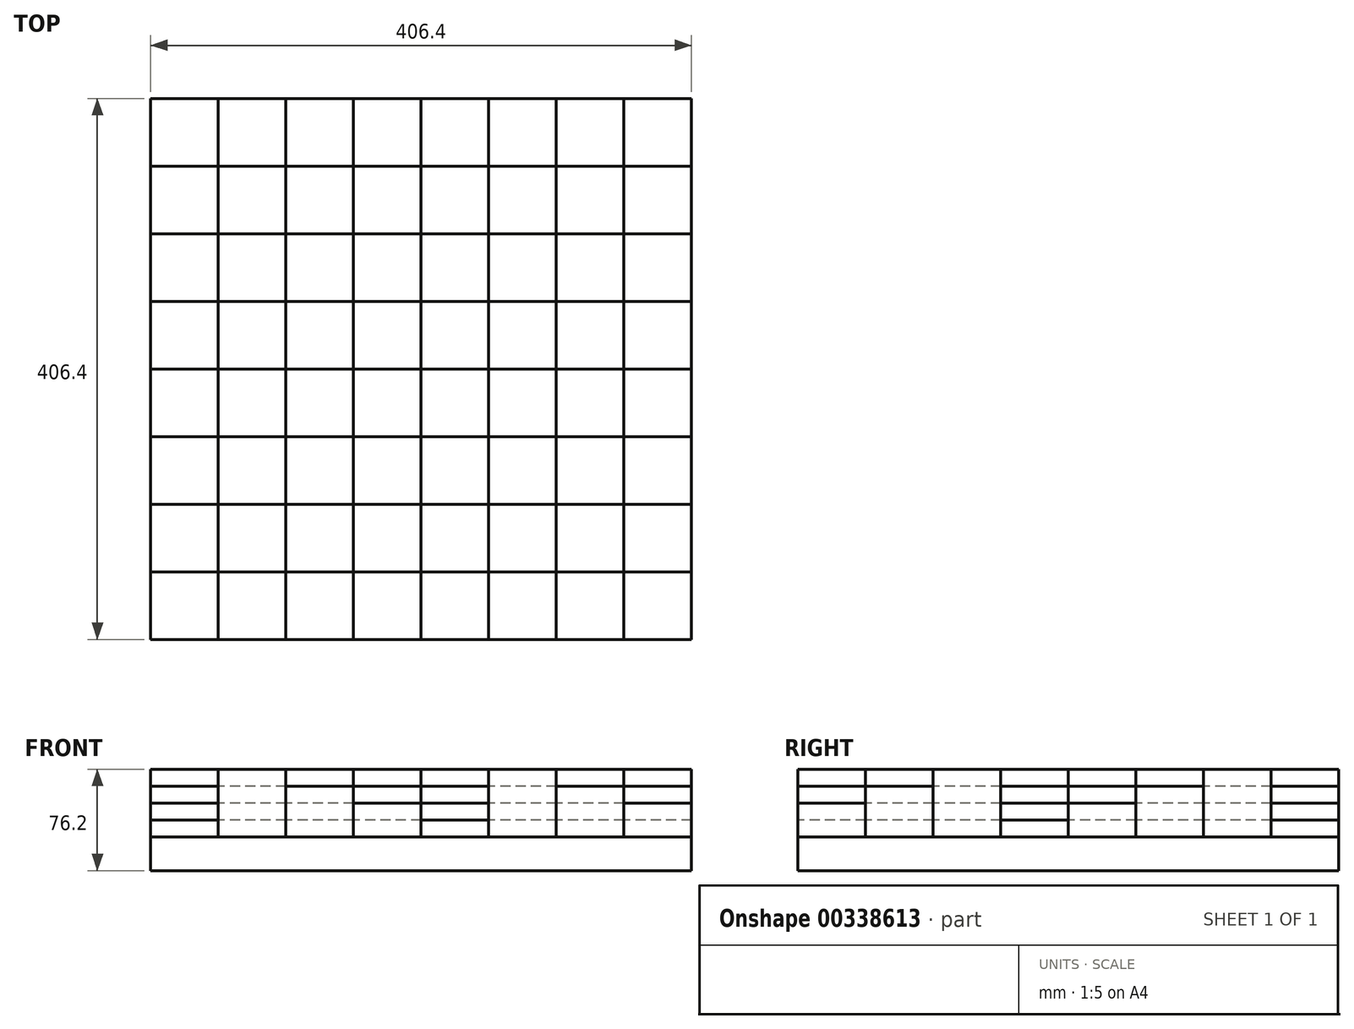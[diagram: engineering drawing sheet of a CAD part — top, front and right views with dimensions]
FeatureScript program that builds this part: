
annotation { "Feature Type Name" : "Feature", "Feature Type Description" : "" }
export const myFeature = defineFeature(function(context is Context, id is Id, definition is map)
    precondition{}
    {
        {
            var Q0;
            Q0=qCreatedBy(makeId("Top.planeOp"),FACE);
            var sketch = newSketch(context, id + "F0", { "sketchPlane" : qUnion([Q0])});
            skLineSegment(sketch, "E0.bottom", {"start": v(203.2, -203.2) * mm, "end": v(-203.2, -203.2) * mm});
            skLineSegment(sketch, "E0.top", {"start": v(203.2, 203.2) * mm, "end": v(-203.2, 203.2) * mm});
            skLineSegment(sketch, "E0.left", {"start": v(203.2, -203.2) * mm, "end": v(203.2, 203.2) * mm});
            skLineSegment(sketch, "E0.right", {"start": v(-203.2, -203.2) * mm, "end": v(-203.2, 203.2) * mm});
            skPoint(sketch, "E0.middle", {"position": v(0, 0) * mm});
            skSolve(sketch);
        }
        {
            var Q0;
            Q0=makeQuery(id+"F0.imprint","IMPRINT",FACE,{"disambiguationData":[TD([[makeQuery(id+"F0.imprint","IMPRINT",EDGE,{"derivedFrom":sQuery(id+"F0.wireOp",EDGE,"E0.bottom")}),-1.0]])]});
            extrude(context, id + "F1", {"entities" : qUnion([Q0]), "depth" : 25.4 * mm});
        }
        {
            var Q0;
            Q0=qCreatedBy(makeId("Right.planeOp"),FACE);
            var sketch = newSketch(context, id + "F2", { "sketchPlane" : qUnion([Q0])});
            skLineSegment(sketch, "E1", {"start": v(203.2, 25.4) * mm, "end": v(203.2, 76.2) * mm});
            skLineSegment(sketch, "E2", {"start": v(203.2, 76.2) * mm, "end": v(152.4, 76.2) * mm});
            skLineSegment(sketch, "E3", {"start": v(152.4, 76.2) * mm, "end": v(152.4, 25.4) * mm});
            skLineSegment(sketch, "E4", {"start": v(152.4, 25.4) * mm, "end": v(203.2, 25.4) * mm});
            skLineSegment(sketch, "E5", {"start": v(152.4, 63.5) * mm, "end": v(101.6, 63.5) * mm});
            skLineSegment(sketch, "E6", {"start": v(101.6, 63.5) * mm, "end": v(101.6, 25.4) * mm});
            skLineSegment(sketch, "E7", {"start": v(101.6, 25.4) * mm, "end": v(152.4, 25.4) * mm});
            skLineSegment(sketch, "E8.bottom", {"start": v(101.6, 25.4) * mm, "end": v(50.8, 25.4) * mm});
            skLineSegment(sketch, "E8.top", {"start": v(101.6, 50.8) * mm, "end": v(50.8, 50.8) * mm});
            skLineSegment(sketch, "E8.left", {"start": v(101.6, 25.4) * mm, "end": v(101.6, 50.8) * mm});
            skLineSegment(sketch, "E8.right", {"start": v(50.8, 25.4) * mm, "end": v(50.8, 50.8) * mm});
            skLineSegment(sketch, "E9.bottom", {"start": v(50.8, 25.4) * mm, "end": v(0, 25.4) * mm});
            skLineSegment(sketch, "E9.top", {"start": v(50.8, 38.1) * mm, "end": v(0, 38.1) * mm});
            skLineSegment(sketch, "E9.left", {"start": v(50.8, 25.4) * mm, "end": v(50.8, 38.1) * mm});
            skLineSegment(sketch, "E9.right", {"start": v(0, 25.4) * mm, "end": v(0, 38.1) * mm});
            skLineSegment(sketch, "E10.bottom", {"start": v(0, 25.4) * mm, "end": v(-50.8, 25.4) * mm});
            skLineSegment(sketch, "E10.top", {"start": v(0, 76.2) * mm, "end": v(-50.8, 76.2) * mm});
            skLineSegment(sketch, "E10.left", {"start": v(0, 25.4) * mm, "end": v(0, 76.2) * mm});
            skLineSegment(sketch, "E10.right", {"start": v(-50.8, 25.4) * mm, "end": v(-50.8, 76.2) * mm});
            skLineSegment(sketch, "E11.bottom", {"start": v(-50.8, 25.4) * mm, "end": v(-101.6, 25.4) * mm});
            skLineSegment(sketch, "E11.top", {"start": v(-50.8, 63.5) * mm, "end": v(-101.6, 63.5) * mm});
            skLineSegment(sketch, "E11.left", {"start": v(-50.8, 25.4) * mm, "end": v(-50.8, 63.5) * mm});
            skLineSegment(sketch, "E11.right", {"start": v(-101.6, 25.4) * mm, "end": v(-101.6, 63.5) * mm});
            skLineSegment(sketch, "E12.bottom", {"start": v(-101.6, 25.4) * mm, "end": v(-152.4, 25.4) * mm});
            skLineSegment(sketch, "E12.top", {"start": v(-101.6, 50.8) * mm, "end": v(-152.4, 50.8) * mm});
            skLineSegment(sketch, "E12.left", {"start": v(-101.6, 25.4) * mm, "end": v(-101.6, 50.8) * mm});
            skLineSegment(sketch, "E12.right", {"start": v(-152.4, 25.4) * mm, "end": v(-152.4, 50.8) * mm});
            skPoint(sketch, "E13.oppositeSnap0", {"position": v(-152.4, 38.1) * mm});
            skLineSegment(sketch, "E13.bottom", {"start": v(-152.4, 25.4) * mm, "end": v(-203.2, 25.4) * mm});
            skLineSegment(sketch, "E13.top", {"start": v(-152.4, 38.1) * mm, "end": v(-203.2, 38.1) * mm});
            skLineSegment(sketch, "E13.left", {"start": v(-152.4, 25.4) * mm, "end": v(-152.4, 38.1) * mm});
            skLineSegment(sketch, "E13.right", {"start": v(-203.2, 25.4) * mm, "end": v(-203.2, 38.1) * mm});
            skSolve(sketch);
        }
        {
            var Q0;
            Q0=makeQuery(id+"F2.imprint","IMPRINT",FACE,{"disambiguationData":[TD([[makeQuery(id+"F2.imprint","IMPRINT",EDGE,{"derivedFrom":sQuery(id+"F2.wireOp",EDGE,"E1")}),1.0]])]});
            extrude(context, id + "F3", {"entities" : qUnion([Q0]), "depth" : 50.8 * mm});
        }
        {
            var Q0;
            {var subQ1=sQuery(id+"F2.wireOp",EDGE,"E5");Q0=makeQuery(id+"F2.imprint","IMPRINT",FACE,{"disambiguationData":[TD([[makeQuery(id+"F2.imprint","IMPRINT",EDGE,{"derivedFrom":subQ1}),1.0]])]});}
            extrude(context, id + "F4", {"entities" : qUnion([Q0]), "depth" : 50.8 * mm});
        }
        {
            var Q0;
            Q0=makeQuery(id+"F2.imprint","IMPRINT",FACE,{"disambiguationData":[TD([[makeQuery(id+"F2.imprint","IMPRINT",EDGE,{"derivedFrom":sQuery(id+"F2.wireOp",EDGE,"E8.bottom")}),-1.0]])]});
            extrude(context, id + "F5", {"entities" : qUnion([Q0]), "depth" : 50.8 * mm});
        }
        {
            var Q0;
            Q0=makeQuery(id+"F2.imprint","IMPRINT",FACE,{"disambiguationData":[TD([[makeQuery(id+"F2.imprint","IMPRINT",EDGE,{"derivedFrom":sQuery(id+"F2.wireOp",EDGE,"E9.bottom")}),-1.0]])]});
            extrude(context, id + "F6", {"entities" : qUnion([Q0]), "depth" : 50.8 * mm});
        }
        {
            var Q0;
            Q0=qCreatedBy(makeId("Right.planeOp"),FACE);
            cPlane(context, id + "F7", {"entities" : qUnion([Q0]), "cplaneType" : CPlaneType.OFFSET, "offset" : 50.8 * mm, "width" : 152.4 * mm, "height" : 152.4 * mm});
        }
        {
            var Q0;
            Q0=qCreatedBy(makeId("Right.planeOp"),FACE);
            cPlane(context, id + "F8", {"entities" : qUnion([Q0]), "cplaneType" : CPlaneType.OFFSET, "offset" : 101.6 * mm, "width" : 152.4 * mm, "height" : 152.4 * mm});
        }
        {
            var Q0;
            Q0=qCreatedBy(makeId("Right.planeOp"),FACE);
            cPlane(context, id + "F9", {"entities" : qUnion([Q0]), "cplaneType" : CPlaneType.OFFSET, "offset" : 152.4 * mm, "width" : 152.4 * mm, "height" : 152.4 * mm});
        }
        {
            var Q0;
            {var subQ0=sQuery(id+"F2.wireOp",EDGE,"E10.bottom");Q0=makeQuery(id+"F2.imprint","IMPRINT",FACE,{"disambiguationData":[TD([[makeQuery(id+"F2.imprint","IMPRINT",EDGE,{"derivedFrom":subQ0}),-1.0]])]});}
            extrude(context, id + "F10", {"entities" : qUnion([Q0]), "depth" : 50.8 * mm});
        }
        {
            var Q0;
            {var subQ3=sQuery(id+"F2.wireOp",EDGE,"E11.bottom");Q0=makeQuery(id+"F2.imprint","IMPRINT",FACE,{"disambiguationData":[TD([[makeQuery(id+"F2.imprint","IMPRINT",EDGE,{"derivedFrom":subQ3}),-1.0]])]});}
            extrude(context, id + "F11", {"entities" : qUnion([Q0]), "depth" : 50.8 * mm});
        }
        {
            var Q0;
            {var subQ3=sQuery(id+"F2.wireOp",EDGE,"E13.bottom");Q0=makeQuery(id+"F2.imprint","IMPRINT",FACE,{"disambiguationData":[TD([[makeQuery(id+"F2.imprint","IMPRINT",EDGE,{"derivedFrom":subQ3}),-1.0]])]});}
            extrude(context, id + "F12", {"entities" : qUnion([Q0]), "depth" : 50.8 * mm});
        }
        {
            var Q0;
            {var subQ3=sQuery(id+"F2.wireOp",EDGE,"E12.bottom");Q0=makeQuery(id+"F2.imprint","IMPRINT",FACE,{"disambiguationData":[TD([[makeQuery(id+"F2.imprint","IMPRINT",EDGE,{"derivedFrom":subQ3}),-1.0]])]});}
            extrude(context, id + "F13", {"entities" : qUnion([Q0]), "depth" : 50.8 * mm});
        }
        {
            var Q0;
            Q0=qCreatedBy(id+"F7.planeOp",FACE);
            var sketch = newSketch(context, id + "F14", { "sketchPlane" : qUnion([Q0])});
            skLineSegment(sketch, "E14", {"start": v(203.2, 25.4) * mm, "end": v(203.2, 63.5) * mm});
            skLineSegment(sketch, "E15", {"start": v(203.2, 63.5) * mm, "end": v(152.4, 63.5) * mm});
            skLineSegment(sketch, "E16", {"start": v(152.4, 63.5) * mm, "end": v(152.4, 25.4) * mm});
            skLineSegment(sketch, "E17", {"start": v(152.4, 25.4) * mm, "end": v(203.2, 25.4) * mm});
            skLineSegment(sketch, "E18", {"start": v(152.4, 50.8) * mm, "end": v(101.6, 50.8) * mm});
            skLineSegment(sketch, "E19", {"start": v(101.6, 50.8) * mm, "end": v(101.6, 25.4) * mm});
            skLineSegment(sketch, "E20", {"start": v(101.6, 25.4) * mm, "end": v(152.4, 25.4) * mm});
            skLineSegment(sketch, "E21.bottom", {"start": v(101.6, 25.4) * mm, "end": v(50.8, 25.4) * mm});
            skLineSegment(sketch, "E21.top", {"start": v(101.6, 38.1) * mm, "end": v(50.8, 38.1) * mm});
            skLineSegment(sketch, "E21.left", {"start": v(101.6, 25.4) * mm, "end": v(101.6, 38.1) * mm});
            skLineSegment(sketch, "E21.right", {"start": v(50.8, 25.4) * mm, "end": v(50.8, 38.1) * mm});
            skLineSegment(sketch, "E22.bottom", {"start": v(50.8, 25.4) * mm, "end": v(0, 25.4) * mm});
            skLineSegment(sketch, "E22.top", {"start": v(50.8, 76.2) * mm, "end": v(0, 76.2) * mm});
            skLineSegment(sketch, "E22.left", {"start": v(50.8, 25.4) * mm, "end": v(50.8, 76.2) * mm});
            skLineSegment(sketch, "E22.right", {"start": v(0, 25.4) * mm, "end": v(0, 76.2) * mm});
            skLineSegment(sketch, "E23.bottom", {"start": v(0, 25.4) * mm, "end": v(-50.8, 25.4) * mm});
            skLineSegment(sketch, "E23.top", {"start": v(0, 63.5) * mm, "end": v(-50.8, 63.5) * mm});
            skLineSegment(sketch, "E23.left", {"start": v(0, 25.4) * mm, "end": v(0, 63.5) * mm});
            skLineSegment(sketch, "E23.right", {"start": v(-50.8, 25.4) * mm, "end": v(-50.8, 63.5) * mm});
            skLineSegment(sketch, "E24.bottom", {"start": v(-50.8, 25.4) * mm, "end": v(-101.6, 25.4) * mm});
            skLineSegment(sketch, "E24.top", {"start": v(-50.8, 50.8) * mm, "end": v(-101.6, 50.8) * mm});
            skLineSegment(sketch, "E24.left", {"start": v(-50.8, 25.4) * mm, "end": v(-50.8, 50.8) * mm});
            skLineSegment(sketch, "E24.right", {"start": v(-101.6, 25.4) * mm, "end": v(-101.6, 50.8) * mm});
            skLineSegment(sketch, "E25.bottom", {"start": v(-101.6, 25.4) * mm, "end": v(-152.4, 25.4) * mm});
            skLineSegment(sketch, "E25.top", {"start": v(-101.6, 38.1) * mm, "end": v(-152.4, 38.1) * mm});
            skLineSegment(sketch, "E25.left", {"start": v(-101.6, 25.4) * mm, "end": v(-101.6, 38.1) * mm});
            skLineSegment(sketch, "E25.right", {"start": v(-152.4, 25.4) * mm, "end": v(-152.4, 38.1) * mm});
            skPoint(sketch, "E26.oppositeSnap0", {"position": v(-152.4, 31.75) * mm});
            skLineSegment(sketch, "E26.bottom", {"start": v(-152.4, 25.4) * mm, "end": v(-203.2, 25.4) * mm});
            skLineSegment(sketch, "E26.top", {"start": v(-152.4, 76.2) * mm, "end": v(-203.2, 76.2) * mm});
            skLineSegment(sketch, "E26.left", {"start": v(-152.4, 25.4) * mm, "end": v(-152.4, 76.2) * mm});
            skLineSegment(sketch, "E26.right", {"start": v(-203.2, 25.4) * mm, "end": v(-203.2, 76.2) * mm});
            skSolve(sketch);
        }
        {
            var Q0;
            Q0=makeQuery(id+"F14.imprint","IMPRINT",FACE,{"disambiguationData":[TD([[makeQuery(id+"F14.imprint","IMPRINT",EDGE,{"derivedFrom":sQuery(id+"F14.wireOp",EDGE,"E14")}),1.0]])]});
            extrude(context, id + "F15", {"entities" : qUnion([Q0]), "depth" : 50.8 * mm});
        }
        {
            var Q0;
            {var subQ1=sQuery(id+"F14.wireOp",EDGE,"E18");Q0=makeQuery(id+"F14.imprint","IMPRINT",FACE,{"disambiguationData":[TD([[makeQuery(id+"F14.imprint","IMPRINT",EDGE,{"derivedFrom":subQ1}),1.0]])]});}
            extrude(context, id + "F16", {"entities" : qUnion([Q0]), "depth" : 50.8 * mm});
        }
        {
            var Q0;
            {var subQ0=sQuery(id+"F14.wireOp",EDGE,"E21.bottom");Q0=makeQuery(id+"F14.imprint","IMPRINT",FACE,{"disambiguationData":[TD([[makeQuery(id+"F14.imprint","IMPRINT",EDGE,{"derivedFrom":subQ0}),-1.0]])]});}
            extrude(context, id + "F17", {"entities" : qUnion([Q0]), "depth" : 50.8 * mm});
        }
        {
            var Q0;
            {var subQ3=sQuery(id+"F14.wireOp",EDGE,"E22.bottom");Q0=makeQuery(id+"F14.imprint","IMPRINT",FACE,{"disambiguationData":[TD([[makeQuery(id+"F14.imprint","IMPRINT",EDGE,{"derivedFrom":subQ3}),-1.0]])]});}
            extrude(context, id + "F18", {"entities" : qUnion([Q0]), "depth" : 50.8 * mm});
        }
        {
            var Q0;
            Q0=makeQuery(id+"F14.imprint","IMPRINT",FACE,{"disambiguationData":[TD([[makeQuery(id+"F14.imprint","IMPRINT",EDGE,{"derivedFrom":sQuery(id+"F14.wireOp",EDGE,"E23.bottom")}),-1.0]])]});
            extrude(context, id + "F19", {"entities" : qUnion([Q0]), "depth" : 50.8 * mm});
        }
        {
            var Q0;
            Q0=makeQuery(id+"F14.imprint","IMPRINT",FACE,{"disambiguationData":[TD([[makeQuery(id+"F14.imprint","IMPRINT",EDGE,{"derivedFrom":sQuery(id+"F14.wireOp",EDGE,"E24.bottom")}),-1.0]])]});
            extrude(context, id + "F20", {"entities" : qUnion([Q0]), "depth" : 50.8 * mm});
        }
        {
            var Q0;
            {var subQ0=sQuery(id+"F14.wireOp",EDGE,"E25.bottom");Q0=makeQuery(id+"F14.imprint","IMPRINT",FACE,{"disambiguationData":[TD([[makeQuery(id+"F14.imprint","IMPRINT",EDGE,{"derivedFrom":subQ0}),-1.0]])]});}
            extrude(context, id + "F21", {"entities" : qUnion([Q0]), "depth" : 50.8 * mm});
        }
        {
            var Q0;
            {var subQ3=sQuery(id+"F14.wireOp",EDGE,"E26.bottom");Q0=makeQuery(id+"F14.imprint","IMPRINT",FACE,{"disambiguationData":[TD([[makeQuery(id+"F14.imprint","IMPRINT",EDGE,{"derivedFrom":subQ3}),-1.0]])]});}
            extrude(context, id + "F22", {"entities" : qUnion([Q0]), "depth" : 50.8 * mm});
        }
        {
            var Q0;
            Q0=qCreatedBy(id+"F8.planeOp",FACE);
            var sketch = newSketch(context, id + "F23", { "sketchPlane" : qUnion([Q0])});
            skLineSegment(sketch, "E27", {"start": v(203.2, 25.4) * mm, "end": v(203.2, 50.8) * mm});
            skLineSegment(sketch, "E28", {"start": v(203.2, 50.8) * mm, "end": v(152.4, 50.8) * mm});
            skLineSegment(sketch, "E29", {"start": v(152.4, 50.8) * mm, "end": v(152.4, 25.4) * mm});
            skLineSegment(sketch, "E30", {"start": v(152.4, 25.4) * mm, "end": v(203.2, 25.4) * mm});
            skLineSegment(sketch, "E31", {"start": v(152.4, 38.1) * mm, "end": v(101.6, 38.1) * mm});
            skLineSegment(sketch, "E32", {"start": v(101.6, 38.1) * mm, "end": v(101.6, 25.4) * mm});
            skLineSegment(sketch, "E33", {"start": v(101.6, 25.4) * mm, "end": v(152.4, 25.4) * mm});
            skLineSegment(sketch, "E34.bottom", {"start": v(101.6, 25.4) * mm, "end": v(50.8, 25.4) * mm});
            skLineSegment(sketch, "E34.top", {"start": v(101.6, 76.2) * mm, "end": v(50.8, 76.2) * mm});
            skLineSegment(sketch, "E34.left", {"start": v(101.6, 25.4) * mm, "end": v(101.6, 76.2) * mm});
            skLineSegment(sketch, "E34.right", {"start": v(50.8, 25.4) * mm, "end": v(50.8, 76.2) * mm});
            skLineSegment(sketch, "E35.bottom", {"start": v(50.8, 25.4) * mm, "end": v(0, 25.4) * mm});
            skLineSegment(sketch, "E35.top", {"start": v(50.8, 63.5) * mm, "end": v(0, 63.5) * mm});
            skLineSegment(sketch, "E35.left", {"start": v(50.8, 25.4) * mm, "end": v(50.8, 63.5) * mm});
            skLineSegment(sketch, "E35.right", {"start": v(0, 25.4) * mm, "end": v(0, 63.5) * mm});
            skLineSegment(sketch, "E36.bottom", {"start": v(0, 25.4) * mm, "end": v(-50.8, 25.4) * mm});
            skLineSegment(sketch, "E36.top", {"start": v(0, 50.8) * mm, "end": v(-50.8, 50.8) * mm});
            skLineSegment(sketch, "E36.left", {"start": v(0, 25.4) * mm, "end": v(0, 50.8) * mm});
            skLineSegment(sketch, "E36.right", {"start": v(-50.8, 25.4) * mm, "end": v(-50.8, 50.8) * mm});
            skLineSegment(sketch, "E37.bottom", {"start": v(-50.8, 25.4) * mm, "end": v(-101.6, 25.4) * mm});
            skLineSegment(sketch, "E37.top", {"start": v(-50.8, 38.1) * mm, "end": v(-101.6, 38.1) * mm});
            skLineSegment(sketch, "E37.left", {"start": v(-50.8, 25.4) * mm, "end": v(-50.8, 38.1) * mm});
            skLineSegment(sketch, "E37.right", {"start": v(-101.6, 25.4) * mm, "end": v(-101.6, 38.1) * mm});
            skLineSegment(sketch, "E38.bottom", {"start": v(-101.6, 25.4) * mm, "end": v(-152.4, 25.4) * mm});
            skLineSegment(sketch, "E38.top", {"start": v(-101.6, 76.2) * mm, "end": v(-152.4, 76.2) * mm});
            skLineSegment(sketch, "E38.left", {"start": v(-101.6, 25.4) * mm, "end": v(-101.6, 76.2) * mm});
            skLineSegment(sketch, "E38.right", {"start": v(-152.4, 25.4) * mm, "end": v(-152.4, 76.2) * mm});
            skPoint(sketch, "E39.oppositeSnap0", {"position": v(-152.4, 50.8) * mm});
            skLineSegment(sketch, "E39.bottom", {"start": v(-152.4, 25.4) * mm, "end": v(-203.2, 25.4) * mm});
            skLineSegment(sketch, "E39.top", {"start": v(-152.4, 63.5) * mm, "end": v(-203.2, 63.5) * mm});
            skLineSegment(sketch, "E39.left", {"start": v(-152.4, 25.4) * mm, "end": v(-152.4, 63.5) * mm});
            skLineSegment(sketch, "E39.right", {"start": v(-203.2, 25.4) * mm, "end": v(-203.2, 63.5) * mm});
            skSolve(sketch);
        }
        {
            var Q0;
            Q0=makeQuery(id+"F23.imprint","IMPRINT",FACE,{"disambiguationData":[TD([[makeQuery(id+"F23.imprint","IMPRINT",EDGE,{"derivedFrom":sQuery(id+"F23.wireOp",EDGE,"E27")}),1.0]])]});
            var Q1;
            {var subQ3=sQuery(id+"F23.wireOp",EDGE,"E34.bottom");Q1=makeQuery(id+"F23.imprint","IMPRINT",FACE,{"disambiguationData":[TD([[makeQuery(id+"F23.imprint","IMPRINT",EDGE,{"derivedFrom":subQ3}),-1.0]])]});}
            var Q2;
            Q2=makeQuery(id+"F23.imprint","IMPRINT",FACE,{"disambiguationData":[TD([[makeQuery(id+"F23.imprint","IMPRINT",EDGE,{"derivedFrom":sQuery(id+"F23.wireOp",EDGE,"E36.bottom")}),-1.0]])]});
            var Q3;
            {var subQ3=sQuery(id+"F23.wireOp",EDGE,"E38.bottom");Q3=makeQuery(id+"F23.imprint","IMPRINT",FACE,{"disambiguationData":[TD([[makeQuery(id+"F23.imprint","IMPRINT",EDGE,{"derivedFrom":subQ3}),-1.0]])]});}
            extrude(context, id + "F24", {"entities" : qUnion([Q0, Q1, Q2, Q3]), "depth" : 50.8 * mm});
        }
        {
            var Q0;
            {var subQ2=sQuery(id+"F23.wireOp",EDGE,"E31");Q0=makeQuery(id+"F23.imprint","IMPRINT",FACE,{"disambiguationData":[TD([[makeQuery(id+"F23.imprint","IMPRINT",EDGE,{"derivedFrom":subQ2}),1.0]])]});}
            var Q1;
            Q1=makeQuery(id+"F23.imprint","IMPRINT",FACE,{"disambiguationData":[TD([[makeQuery(id+"F23.imprint","IMPRINT",EDGE,{"derivedFrom":sQuery(id+"F23.wireOp",EDGE,"E35.bottom")}),-1.0]])]});
            var Q2;
            {var subQ0=sQuery(id+"F23.wireOp",EDGE,"E37.bottom");Q2=makeQuery(id+"F23.imprint","IMPRINT",FACE,{"disambiguationData":[TD([[makeQuery(id+"F23.imprint","IMPRINT",EDGE,{"derivedFrom":subQ0}),-1.0]])]});}
            var Q3;
            Q3=makeQuery(id+"F23.imprint","IMPRINT",FACE,{"disambiguationData":[TD([[makeQuery(id+"F23.imprint","IMPRINT",EDGE,{"derivedFrom":sQuery(id+"F23.wireOp",EDGE,"E39.bottom")}),-1.0]])]});
            extrude(context, id + "F25", {"entities" : qUnion([Q0, Q1, Q2, Q3]), "depth" : 50.8 * mm});
        }
        {
            var Q0;
            Q0=qCreatedBy(id+"F9.planeOp",FACE);
            var sketch = newSketch(context, id + "F26", { "sketchPlane" : qUnion([Q0])});
            skLineSegment(sketch, "E40", {"start": v(203.2, 25.4) * mm, "end": v(203.2, 38.1) * mm});
            skLineSegment(sketch, "E41", {"start": v(203.2, 38.1) * mm, "end": v(152.4, 38.1) * mm});
            skLineSegment(sketch, "E42", {"start": v(152.4, 38.1) * mm, "end": v(152.4, 25.4) * mm});
            skLineSegment(sketch, "E43", {"start": v(152.4, 25.4) * mm, "end": v(203.2, 25.4) * mm});
            skLineSegment(sketch, "E44", {"start": v(152.4, 76.2) * mm, "end": v(101.6, 76.2) * mm});
            skLineSegment(sketch, "E45", {"start": v(101.6, 76.2) * mm, "end": v(101.6, 25.4) * mm});
            skLineSegment(sketch, "E46", {"start": v(101.6, 25.4) * mm, "end": v(152.4, 25.4) * mm});
            skLineSegment(sketch, "E47.bottom", {"start": v(101.6, 25.4) * mm, "end": v(50.8, 25.4) * mm});
            skLineSegment(sketch, "E47.top", {"start": v(101.6, 63.5) * mm, "end": v(50.8, 63.5) * mm});
            skLineSegment(sketch, "E47.left", {"start": v(101.6, 25.4) * mm, "end": v(101.6, 63.5) * mm});
            skLineSegment(sketch, "E47.right", {"start": v(50.8, 25.4) * mm, "end": v(50.8, 63.5) * mm});
            skLineSegment(sketch, "E48.bottom", {"start": v(50.8, 25.4) * mm, "end": v(0, 25.4) * mm});
            skLineSegment(sketch, "E48.top", {"start": v(50.8, 50.8) * mm, "end": v(0, 50.8) * mm});
            skLineSegment(sketch, "E48.left", {"start": v(50.8, 25.4) * mm, "end": v(50.8, 50.8) * mm});
            skLineSegment(sketch, "E48.right", {"start": v(0, 25.4) * mm, "end": v(0, 50.8) * mm});
            skLineSegment(sketch, "E49.bottom", {"start": v(0, 25.4) * mm, "end": v(-50.8, 25.4) * mm});
            skLineSegment(sketch, "E49.top", {"start": v(0, 38.1) * mm, "end": v(-50.8, 38.1) * mm});
            skLineSegment(sketch, "E49.left", {"start": v(0, 25.4) * mm, "end": v(0, 38.1) * mm});
            skLineSegment(sketch, "E49.right", {"start": v(-50.8, 25.4) * mm, "end": v(-50.8, 38.1) * mm});
            skLineSegment(sketch, "E50.bottom", {"start": v(-50.8, 25.4) * mm, "end": v(-101.6, 25.4) * mm});
            skLineSegment(sketch, "E50.top", {"start": v(-50.8, 76.2) * mm, "end": v(-101.6, 76.2) * mm});
            skLineSegment(sketch, "E50.left", {"start": v(-50.8, 25.4) * mm, "end": v(-50.8, 76.2) * mm});
            skLineSegment(sketch, "E50.right", {"start": v(-101.6, 25.4) * mm, "end": v(-101.6, 76.2) * mm});
            skLineSegment(sketch, "E51.bottom", {"start": v(-101.6, 25.4) * mm, "end": v(-152.4, 25.4) * mm});
            skLineSegment(sketch, "E51.top", {"start": v(-101.6, 63.5) * mm, "end": v(-152.4, 63.5) * mm});
            skLineSegment(sketch, "E51.left", {"start": v(-101.6, 25.4) * mm, "end": v(-101.6, 63.5) * mm});
            skLineSegment(sketch, "E51.right", {"start": v(-152.4, 25.4) * mm, "end": v(-152.4, 63.5) * mm});
            skPoint(sketch, "E52.oppositeSnap0", {"position": v(-152.4, 44.45) * mm});
            skLineSegment(sketch, "E52.bottom", {"start": v(-152.4, 25.4) * mm, "end": v(-203.2, 25.4) * mm});
            skLineSegment(sketch, "E52.top", {"start": v(-152.4, 50.8) * mm, "end": v(-203.2, 50.8) * mm});
            skLineSegment(sketch, "E52.left", {"start": v(-152.4, 25.4) * mm, "end": v(-152.4, 50.8) * mm});
            skLineSegment(sketch, "E52.right", {"start": v(-203.2, 25.4) * mm, "end": v(-203.2, 50.8) * mm});
            skLineSegment(sketch, "E53", {"start": v(152.4, 38.1) * mm, "end": v(152.4, 76.2) * mm});
            skSolve(sketch);
        }
        {
            var Q0;
            Q0=makeQuery(id+"F26.imprint","IMPRINT",FACE,{"disambiguationData":[TD([[makeQuery(id+"F26.imprint","IMPRINT",EDGE,{"derivedFrom":sQuery(id+"F26.wireOp",EDGE,"E40")}),1.0]])]});
            var Q1;
            Q1=makeQuery(id+"F26.imprint","IMPRINT",FACE,{"disambiguationData":[TD([[makeQuery(id+"F26.imprint","IMPRINT",EDGE,{"derivedFrom":sQuery(id+"F26.wireOp",EDGE,"E47.bottom")}),-1.0]])]});
            var Q2;
            {var subQ0=sQuery(id+"F26.wireOp",EDGE,"E49.bottom");Q2=makeQuery(id+"F26.imprint","IMPRINT",FACE,{"disambiguationData":[TD([[makeQuery(id+"F26.imprint","IMPRINT",EDGE,{"derivedFrom":subQ0}),-1.0]])]});}
            var Q3;
            Q3=makeQuery(id+"F26.imprint","IMPRINT",FACE,{"disambiguationData":[TD([[makeQuery(id+"F26.imprint","IMPRINT",EDGE,{"derivedFrom":sQuery(id+"F26.wireOp",EDGE,"E51.bottom")}),-1.0]])]});
            extrude(context, id + "F27", {"entities" : qUnion([Q0, Q1, Q2, Q3]), "depth" : 50.8 * mm});
        }
        {
            var Q0;
            Q0=makeQuery(id+"F26.imprint","IMPRINT",FACE,{"disambiguationData":[TD([[makeQuery(id+"F26.imprint","IMPRINT",EDGE,{"derivedFrom":sQuery(id+"F26.wireOp",EDGE,"E42")}),-1.0]])]});
            var Q1;
            Q1=makeQuery(id+"F26.imprint","IMPRINT",FACE,{"disambiguationData":[TD([[makeQuery(id+"F26.imprint","IMPRINT",EDGE,{"derivedFrom":sQuery(id+"F26.wireOp",EDGE,"E48.bottom")}),-1.0]])]});
            var Q2;
            {var subQ3=sQuery(id+"F26.wireOp",EDGE,"E50.bottom");Q2=makeQuery(id+"F26.imprint","IMPRINT",FACE,{"disambiguationData":[TD([[makeQuery(id+"F26.imprint","IMPRINT",EDGE,{"derivedFrom":subQ3}),-1.0]])]});}
            var Q3;
            Q3=makeQuery(id+"F26.imprint","IMPRINT",FACE,{"disambiguationData":[TD([[makeQuery(id+"F26.imprint","IMPRINT",EDGE,{"derivedFrom":sQuery(id+"F26.wireOp",EDGE,"E52.bottom")}),-1.0]])]});
            extrude(context, id + "F28", {"entities" : qUnion([Q0, Q1, Q2, Q3]), "depth" : 50.8 * mm});
        }
        {
            var Q0;
            Q0=qCreatedBy(makeId("Right.planeOp"),FACE);
            cPlane(context, id + "F29", {"entities" : qUnion([Q0]), "cplaneType" : CPlaneType.OFFSET, "offset" : 50.8 * mm, "oppositeDirection" : true, "width" : 152.4 * mm, "height" : 152.4 * mm});
        }
        {
            var Q0;
            Q0=qCreatedBy(makeId("Right.planeOp"),FACE);
            cPlane(context, id + "F30", {"entities" : qUnion([Q0]), "cplaneType" : CPlaneType.OFFSET, "offset" : 101.6 * mm, "oppositeDirection" : true, "width" : 152.4 * mm, "height" : 152.4 * mm});
        }
        {
            var Q0;
            Q0=qCreatedBy(makeId("Right.planeOp"),FACE);
            cPlane(context, id + "F31", {"entities" : qUnion([Q0]), "cplaneType" : CPlaneType.OFFSET, "offset" : 152.4 * mm, "oppositeDirection" : true, "width" : 152.4 * mm, "height" : 152.4 * mm});
        }
        {
            var Q0;
            Q0=qCreatedBy(id+"F29.planeOp",FACE);
            var sketch = newSketch(context, id + "F32", { "sketchPlane" : qUnion([Q0])});
            skLineSegment(sketch, "E54", {"start": v(203.2, 25.4) * mm, "end": v(203.2, 38.1) * mm});
            skLineSegment(sketch, "E55", {"start": v(203.2, 38.1) * mm, "end": v(152.4, 38.1) * mm});
            skLineSegment(sketch, "E56", {"start": v(152.4, 38.1) * mm, "end": v(152.4, 25.4) * mm});
            skLineSegment(sketch, "E57", {"start": v(152.4, 25.4) * mm, "end": v(203.2, 25.4) * mm});
            skLineSegment(sketch, "E58", {"start": v(152.4, 76.2) * mm, "end": v(101.6, 76.2) * mm});
            skLineSegment(sketch, "E59", {"start": v(101.6, 76.2) * mm, "end": v(101.6, 25.4) * mm});
            skLineSegment(sketch, "E60", {"start": v(101.6, 25.4) * mm, "end": v(152.4, 25.4) * mm});
            skLineSegment(sketch, "E61.bottom", {"start": v(101.6, 25.4) * mm, "end": v(50.8, 25.4) * mm});
            skLineSegment(sketch, "E61.top", {"start": v(101.6, 63.5) * mm, "end": v(50.8, 63.5) * mm});
            skLineSegment(sketch, "E61.left", {"start": v(101.6, 25.4) * mm, "end": v(101.6, 63.5) * mm});
            skLineSegment(sketch, "E61.right", {"start": v(50.8, 25.4) * mm, "end": v(50.8, 63.5) * mm});
            skLineSegment(sketch, "E62.bottom", {"start": v(50.8, 25.4) * mm, "end": v(0, 25.4) * mm});
            skLineSegment(sketch, "E62.top", {"start": v(50.8, 50.8) * mm, "end": v(0, 50.8) * mm});
            skLineSegment(sketch, "E62.left", {"start": v(50.8, 25.4) * mm, "end": v(50.8, 50.8) * mm});
            skLineSegment(sketch, "E62.right", {"start": v(0, 25.4) * mm, "end": v(0, 50.8) * mm});
            skLineSegment(sketch, "E63.bottom", {"start": v(0, 25.4) * mm, "end": v(-50.8, 25.4) * mm});
            skLineSegment(sketch, "E63.top", {"start": v(0, 38.1) * mm, "end": v(-50.8, 38.1) * mm});
            skLineSegment(sketch, "E63.left", {"start": v(0, 25.4) * mm, "end": v(0, 38.1) * mm});
            skLineSegment(sketch, "E63.right", {"start": v(-50.8, 25.4) * mm, "end": v(-50.8, 38.1) * mm});
            skLineSegment(sketch, "E64.bottom", {"start": v(-50.8, 25.4) * mm, "end": v(-101.6, 25.4) * mm});
            skLineSegment(sketch, "E64.top", {"start": v(-50.8, 76.2) * mm, "end": v(-101.6, 76.2) * mm});
            skLineSegment(sketch, "E64.left", {"start": v(-50.8, 25.4) * mm, "end": v(-50.8, 76.2) * mm});
            skLineSegment(sketch, "E64.right", {"start": v(-101.6, 25.4) * mm, "end": v(-101.6, 76.2) * mm});
            skLineSegment(sketch, "E65.bottom", {"start": v(-101.6, 25.4) * mm, "end": v(-152.4, 25.4) * mm});
            skLineSegment(sketch, "E65.top", {"start": v(-101.6, 63.5) * mm, "end": v(-152.4, 63.5) * mm});
            skLineSegment(sketch, "E65.left", {"start": v(-101.6, 25.4) * mm, "end": v(-101.6, 63.5) * mm});
            skLineSegment(sketch, "E65.right", {"start": v(-152.4, 25.4) * mm, "end": v(-152.4, 63.5) * mm});
            skPoint(sketch, "E66.oppositeSnap0", {"position": v(-152.4, 44.45) * mm});
            skLineSegment(sketch, "E66.bottom", {"start": v(-152.4, 25.4) * mm, "end": v(-203.2, 25.4) * mm});
            skLineSegment(sketch, "E66.top", {"start": v(-152.4, 50.8) * mm, "end": v(-203.2, 50.8) * mm});
            skLineSegment(sketch, "E66.left", {"start": v(-152.4, 25.4) * mm, "end": v(-152.4, 50.8) * mm});
            skLineSegment(sketch, "E66.right", {"start": v(-203.2, 25.4) * mm, "end": v(-203.2, 50.8) * mm});
            skLineSegment(sketch, "E67", {"start": v(152.4, 38.1) * mm, "end": v(152.4, 76.2) * mm});
            skSolve(sketch);
        }
        {
            var Q0;
            Q0=qCreatedBy(id+"F30.planeOp",FACE);
            var sketch = newSketch(context, id + "F33", { "sketchPlane" : qUnion([Q0])});
            skLineSegment(sketch, "E68", {"start": v(203.2, 25.4) * mm, "end": v(203.2, 50.8) * mm});
            skLineSegment(sketch, "E69", {"start": v(203.2, 50.8) * mm, "end": v(152.4, 50.8) * mm});
            skLineSegment(sketch, "E70", {"start": v(152.4, 50.8) * mm, "end": v(152.4, 25.4) * mm});
            skLineSegment(sketch, "E71", {"start": v(152.4, 25.4) * mm, "end": v(203.2, 25.4) * mm});
            skLineSegment(sketch, "E72", {"start": v(152.4, 38.1) * mm, "end": v(101.6, 38.1) * mm});
            skLineSegment(sketch, "E73", {"start": v(101.6, 38.1) * mm, "end": v(101.6, 25.4) * mm});
            skLineSegment(sketch, "E74", {"start": v(101.6, 25.4) * mm, "end": v(152.4, 25.4) * mm});
            skLineSegment(sketch, "E75.bottom", {"start": v(101.6, 25.4) * mm, "end": v(50.8, 25.4) * mm});
            skLineSegment(sketch, "E75.top", {"start": v(101.6, 76.2) * mm, "end": v(50.8, 76.2) * mm});
            skLineSegment(sketch, "E75.left", {"start": v(101.6, 25.4) * mm, "end": v(101.6, 76.2) * mm});
            skLineSegment(sketch, "E75.right", {"start": v(50.8, 25.4) * mm, "end": v(50.8, 76.2) * mm});
            skLineSegment(sketch, "E76.bottom", {"start": v(50.8, 25.4) * mm, "end": v(0, 25.4) * mm});
            skLineSegment(sketch, "E76.top", {"start": v(50.8, 63.5) * mm, "end": v(0, 63.5) * mm});
            skLineSegment(sketch, "E76.left", {"start": v(50.8, 25.4) * mm, "end": v(50.8, 63.5) * mm});
            skLineSegment(sketch, "E76.right", {"start": v(0, 25.4) * mm, "end": v(0, 63.5) * mm});
            skLineSegment(sketch, "E77.bottom", {"start": v(0, 25.4) * mm, "end": v(-50.8, 25.4) * mm});
            skLineSegment(sketch, "E77.top", {"start": v(0, 50.8) * mm, "end": v(-50.8, 50.8) * mm});
            skLineSegment(sketch, "E77.left", {"start": v(0, 25.4) * mm, "end": v(0, 50.8) * mm});
            skLineSegment(sketch, "E77.right", {"start": v(-50.8, 25.4) * mm, "end": v(-50.8, 50.8) * mm});
            skLineSegment(sketch, "E78.bottom", {"start": v(-50.8, 25.4) * mm, "end": v(-101.6, 25.4) * mm});
            skLineSegment(sketch, "E78.top", {"start": v(-50.8, 38.1) * mm, "end": v(-101.6, 38.1) * mm});
            skLineSegment(sketch, "E78.left", {"start": v(-50.8, 25.4) * mm, "end": v(-50.8, 38.1) * mm});
            skLineSegment(sketch, "E78.right", {"start": v(-101.6, 25.4) * mm, "end": v(-101.6, 38.1) * mm});
            skLineSegment(sketch, "E79.bottom", {"start": v(-101.6, 25.4) * mm, "end": v(-152.4, 25.4) * mm});
            skLineSegment(sketch, "E79.top", {"start": v(-101.6, 76.2) * mm, "end": v(-152.4, 76.2) * mm});
            skLineSegment(sketch, "E79.left", {"start": v(-101.6, 25.4) * mm, "end": v(-101.6, 76.2) * mm});
            skLineSegment(sketch, "E79.right", {"start": v(-152.4, 25.4) * mm, "end": v(-152.4, 76.2) * mm});
            skPoint(sketch, "E80.oppositeSnap0", {"position": v(-152.4, 50.8) * mm});
            skLineSegment(sketch, "E80.bottom", {"start": v(-152.4, 25.4) * mm, "end": v(-203.2, 25.4) * mm});
            skLineSegment(sketch, "E80.top", {"start": v(-152.4, 63.5) * mm, "end": v(-203.2, 63.5) * mm});
            skLineSegment(sketch, "E80.left", {"start": v(-152.4, 25.4) * mm, "end": v(-152.4, 63.5) * mm});
            skLineSegment(sketch, "E80.right", {"start": v(-203.2, 25.4) * mm, "end": v(-203.2, 63.5) * mm});
            skSolve(sketch);
        }
        {
            var Q0;
            Q0=qCreatedBy(id+"F31.planeOp",FACE);
            var sketch = newSketch(context, id + "F34", { "sketchPlane" : qUnion([Q0])});
            skLineSegment(sketch, "E81", {"start": v(203.2, 25.4) * mm, "end": v(203.2, 63.5) * mm});
            skLineSegment(sketch, "E82", {"start": v(203.2, 63.5) * mm, "end": v(152.4, 63.5) * mm});
            skLineSegment(sketch, "E83", {"start": v(152.4, 63.5) * mm, "end": v(152.4, 25.4) * mm});
            skLineSegment(sketch, "E84", {"start": v(152.4, 25.4) * mm, "end": v(203.2, 25.4) * mm});
            skLineSegment(sketch, "E85", {"start": v(152.4, 50.8) * mm, "end": v(101.6, 50.8) * mm});
            skLineSegment(sketch, "E86", {"start": v(101.6, 50.8) * mm, "end": v(101.6, 25.4) * mm});
            skLineSegment(sketch, "E87", {"start": v(101.6, 25.4) * mm, "end": v(152.4, 25.4) * mm});
            skLineSegment(sketch, "E88.bottom", {"start": v(101.6, 25.4) * mm, "end": v(50.8, 25.4) * mm});
            skLineSegment(sketch, "E88.top", {"start": v(101.6, 38.1) * mm, "end": v(50.8, 38.1) * mm});
            skLineSegment(sketch, "E88.left", {"start": v(101.6, 25.4) * mm, "end": v(101.6, 38.1) * mm});
            skLineSegment(sketch, "E88.right", {"start": v(50.8, 25.4) * mm, "end": v(50.8, 38.1) * mm});
            skLineSegment(sketch, "E89.bottom", {"start": v(50.8, 25.4) * mm, "end": v(0, 25.4) * mm});
            skLineSegment(sketch, "E89.top", {"start": v(50.8, 76.2) * mm, "end": v(0, 76.2) * mm});
            skLineSegment(sketch, "E89.left", {"start": v(50.8, 25.4) * mm, "end": v(50.8, 76.2) * mm});
            skLineSegment(sketch, "E89.right", {"start": v(0, 25.4) * mm, "end": v(0, 76.2) * mm});
            skLineSegment(sketch, "E90.bottom", {"start": v(0, 25.4) * mm, "end": v(-50.8, 25.4) * mm});
            skLineSegment(sketch, "E90.top", {"start": v(0, 63.5) * mm, "end": v(-50.8, 63.5) * mm});
            skLineSegment(sketch, "E90.left", {"start": v(0, 25.4) * mm, "end": v(0, 63.5) * mm});
            skLineSegment(sketch, "E90.right", {"start": v(-50.8, 25.4) * mm, "end": v(-50.8, 63.5) * mm});
            skLineSegment(sketch, "E91.bottom", {"start": v(-50.8, 25.4) * mm, "end": v(-101.6, 25.4) * mm});
            skLineSegment(sketch, "E91.top", {"start": v(-50.8, 50.8) * mm, "end": v(-101.6, 50.8) * mm});
            skLineSegment(sketch, "E91.left", {"start": v(-50.8, 25.4) * mm, "end": v(-50.8, 50.8) * mm});
            skLineSegment(sketch, "E91.right", {"start": v(-101.6, 25.4) * mm, "end": v(-101.6, 50.8) * mm});
            skLineSegment(sketch, "E92.bottom", {"start": v(-101.6, 25.4) * mm, "end": v(-152.4, 25.4) * mm});
            skLineSegment(sketch, "E92.top", {"start": v(-101.6, 38.1) * mm, "end": v(-152.4, 38.1) * mm});
            skLineSegment(sketch, "E92.left", {"start": v(-101.6, 25.4) * mm, "end": v(-101.6, 38.1) * mm});
            skLineSegment(sketch, "E92.right", {"start": v(-152.4, 25.4) * mm, "end": v(-152.4, 38.1) * mm});
            skPoint(sketch, "E93.oppositeSnap0", {"position": v(-152.4, 31.75) * mm});
            skLineSegment(sketch, "E93.bottom", {"start": v(-152.4, 25.4) * mm, "end": v(-203.2, 25.4) * mm});
            skLineSegment(sketch, "E93.top", {"start": v(-152.4, 76.2) * mm, "end": v(-203.2, 76.2) * mm});
            skLineSegment(sketch, "E93.left", {"start": v(-152.4, 25.4) * mm, "end": v(-152.4, 76.2) * mm});
            skLineSegment(sketch, "E93.right", {"start": v(-203.2, 25.4) * mm, "end": v(-203.2, 76.2) * mm});
            skSolve(sketch);
        }
        {
            var Q0;
            Q0=makeQuery(id+"F1.opExtrude","SWEPT_FACE",FACE,{"disambiguationData":[OSD([sQuery(id+"F0.wireOp",EDGE,"E0.right")])]});
            cPlane(context, id + "F35", {"entities" : qUnion([Q0]), "cplaneType" : CPlaneType.OFFSET, "offset" : 0 * mm, "width" : 152.4 * mm, "height" : 152.4 * mm});
        }
        {
            var Q0;
            Q0=qCreatedBy(id+"F35.planeOp",FACE);
            var sketch = newSketch(context, id + "F36", { "sketchPlane" : qUnion([Q0])});
            skLineSegment(sketch, "E94", {"start": v(-203.2, 25.4) * mm, "end": v(-203.2, 76.2) * mm});
            skLineSegment(sketch, "E95.MirrorCS", {"start": v(152.4, 38.1) * mm, "end": v(203.2, 38.1) * mm});
            skLineSegment(sketch, "E96.MirrorCS", {"start": v(152.4, 25.4) * mm, "end": v(152.4, 38.1) * mm});
            skLineSegment(sketch, "E97.MirrorCS", {"start": v(0, 25.4) * mm, "end": v(0, 38.1) * mm});
            skLineSegment(sketch, "E98.MirrorCS", {"start": v(-50.8, 25.4) * mm, "end": v(-50.8, 50.8) * mm});
            skLineSegment(sketch, "E99.MirrorCS", {"start": v(-50.8, 25.4) * mm, "end": v(-50.8, 38.1) * mm});
            skLineSegment(sketch, "E100.MirrorCS", {"start": v(152.4, 25.4) * mm, "end": v(152.4, 50.8) * mm});
            skLineSegment(sketch, "E101.MirrorCS", {"start": v(203.2, 25.4) * mm, "end": v(203.2, 38.1) * mm});
            skLineSegment(sketch, "E102.MirrorCS", {"start": v(-101.6, 25.4) * mm, "end": v(-101.6, 50.8) * mm});
            skLineSegment(sketch, "E103.MirrorCS", {"start": v(101.6, 25.4) * mm, "end": v(101.6, 63.5) * mm});
            skLineSegment(sketch, "E104.MirrorCS", {"start": v(50.8, 25.4) * mm, "end": v(50.8, 63.5) * mm});
            skLineSegment(sketch, "E105.MirrorCS", {"start": v(-101.6, 63.5) * mm, "end": v(-101.6, 25.4) * mm});
            skLineSegment(sketch, "E106.MirrorCS", {"start": v(-50.8, 25.4) * mm, "end": v(0, 25.4) * mm});
            skLineSegment(sketch, "E107.MirrorCS", {"start": v(0, 76.2) * mm, "end": v(50.8, 76.2) * mm});
            skLineSegment(sketch, "E108.MirrorCS", {"start": v(152.4, 25.4) * mm, "end": v(203.2, 25.4) * mm});
            skLineSegment(sketch, "E109.MirrorCS", {"start": v(-50.8, 38.1) * mm, "end": v(0, 38.1) * mm});
            skLineSegment(sketch, "E110.MirrorCS", {"start": v(50.8, 25.4) * mm, "end": v(50.8, 76.2) * mm});
            skLineSegment(sketch, "E111.MirrorCS", {"start": v(50.8, 63.5) * mm, "end": v(101.6, 63.5) * mm});
            skLineSegment(sketch, "E112.MirrorCS", {"start": v(101.6, 25.4) * mm, "end": v(152.4, 25.4) * mm});
            skLineSegment(sketch, "E113.MirrorCS", {"start": v(0, 25.4) * mm, "end": v(50.8, 25.4) * mm});
            skLineSegment(sketch, "E114.MirrorCS", {"start": v(50.8, 25.4) * mm, "end": v(101.6, 25.4) * mm});
            skLineSegment(sketch, "E115.MirrorCS", {"start": v(-101.6, 25.4) * mm, "end": v(-50.8, 25.4) * mm});
            skLineSegment(sketch, "E116.MirrorCS", {"start": v(0, 25.4) * mm, "end": v(0, 76.2) * mm});
            skLineSegment(sketch, "E117.MirrorCS", {"start": v(101.6, 50.8) * mm, "end": v(152.4, 50.8) * mm});
            skLineSegment(sketch, "E118.MirrorCS", {"start": v(-101.6, 25.4) * mm, "end": v(-152.4, 25.4) * mm});
            skPoint(sketch, "E119.MirrorP", {"position": v(152.4, 38.1) * mm});
            skLineSegment(sketch, "E120.MirrorCS", {"start": v(101.6, 25.4) * mm, "end": v(101.6, 50.8) * mm});
            skLineSegment(sketch, "E121.MirrorCS", {"start": v(-101.6, 50.8) * mm, "end": v(-50.8, 50.8) * mm});
            skLineSegment(sketch, "E122.MirrorCS", {"start": v(-152.4, 76.2) * mm, "end": v(-152.4, 25.4) * mm});
            skLineSegment(sketch, "E123.MirrorCS", {"start": v(-152.4, 63.5) * mm, "end": v(-101.6, 63.5) * mm});
            skLineSegment(sketch, "E124.MirrorCS", {"start": v(-203.2, 76.2) * mm, "end": v(-152.4, 76.2) * mm});
            skLineSegment(sketch, "E125.MirrorCS", {"start": v(-152.4, 25.4) * mm, "end": v(-203.2, 25.4) * mm});
            skSolve(sketch);
        }
        {
            var Q0;
            Q0=makeQuery(id+"F36.imprint","IMPRINT",FACE,{"disambiguationData":[TD([[makeQuery(id+"F36.imprint","IMPRINT",EDGE,{"derivedFrom":sQuery(id+"F36.wireOp",EDGE,"E94")}),-1.0]])]});
            var Q1;
            Q1=makeQuery(id+"F33.imprint","IMPRINT",FACE,{"disambiguationData":[TD([[makeQuery(id+"F33.imprint","IMPRINT",EDGE,{"derivedFrom":sQuery(id+"F33.wireOp",EDGE,"E68")}),1.0]])]});
            var Q2;
            {var subQ1=sQuery(id+"F36.wireOp",EDGE,"E115.MirrorCS");Q2=makeQuery(id+"F36.imprint","IMPRINT",FACE,{"disambiguationData":[TD([[makeQuery(id+"F36.imprint","IMPRINT",EDGE,{"derivedFrom":subQ1}),1.0]])]});}
            var Q3;
            {var subQ3=sQuery(id+"F33.wireOp",EDGE,"E75.bottom");Q3=makeQuery(id+"F33.imprint","IMPRINT",FACE,{"disambiguationData":[TD([[makeQuery(id+"F33.imprint","IMPRINT",EDGE,{"derivedFrom":subQ3}),-1.0]])]});}
            var Q4;
            {var subQ1=sQuery(id+"F36.wireOp",EDGE,"E113.MirrorCS");Q4=makeQuery(id+"F36.imprint","IMPRINT",FACE,{"disambiguationData":[TD([[makeQuery(id+"F36.imprint","IMPRINT",EDGE,{"derivedFrom":subQ1}),1.0]])]});}
            var Q5;
            {var subQ2=sQuery(id+"F36.wireOp",EDGE,"E117.MirrorCS");Q5=makeQuery(id+"F36.imprint","IMPRINT",FACE,{"disambiguationData":[TD([[makeQuery(id+"F36.imprint","IMPRINT",EDGE,{"derivedFrom":subQ2}),-1.0]])]});}
            var Q6;
            Q6=makeQuery(id+"F33.imprint","IMPRINT",FACE,{"disambiguationData":[TD([[makeQuery(id+"F33.imprint","IMPRINT",EDGE,{"derivedFrom":sQuery(id+"F33.wireOp",EDGE,"E77.bottom")}),-1.0]])]});
            var Q7;
            {var subQ3=sQuery(id+"F33.wireOp",EDGE,"E79.bottom");Q7=makeQuery(id+"F33.imprint","IMPRINT",FACE,{"disambiguationData":[TD([[makeQuery(id+"F33.imprint","IMPRINT",EDGE,{"derivedFrom":subQ3}),-1.0]])]});}
            var Q8;
            {var subQ1=sQuery(id+"F34.wireOp",EDGE,"E85");Q8=makeQuery(id+"F34.imprint","IMPRINT",FACE,{"disambiguationData":[TD([[makeQuery(id+"F34.imprint","IMPRINT",EDGE,{"derivedFrom":subQ1}),1.0]])]});}
            var Q9;
            {var subQ3=sQuery(id+"F34.wireOp",EDGE,"E89.bottom");Q9=makeQuery(id+"F34.imprint","IMPRINT",FACE,{"disambiguationData":[TD([[makeQuery(id+"F34.imprint","IMPRINT",EDGE,{"derivedFrom":subQ3}),-1.0]])]});}
            var Q10;
            Q10=makeQuery(id+"F34.imprint","IMPRINT",FACE,{"disambiguationData":[TD([[makeQuery(id+"F34.imprint","IMPRINT",EDGE,{"derivedFrom":sQuery(id+"F34.wireOp",EDGE,"E91.bottom")}),-1.0]])]});
            var Q11;
            {var subQ3=sQuery(id+"F34.wireOp",EDGE,"E93.bottom");Q11=makeQuery(id+"F34.imprint","IMPRINT",FACE,{"disambiguationData":[TD([[makeQuery(id+"F34.imprint","IMPRINT",EDGE,{"derivedFrom":subQ3}),-1.0]])]});}
            var Q12;
            Q12=makeQuery(id+"F32.imprint","IMPRINT",FACE,{"disambiguationData":[TD([[makeQuery(id+"F32.imprint","IMPRINT",EDGE,{"derivedFrom":sQuery(id+"F32.wireOp",EDGE,"E56")}),-1.0]])]});
            var Q13;
            Q13=makeQuery(id+"F32.imprint","IMPRINT",FACE,{"disambiguationData":[TD([[makeQuery(id+"F32.imprint","IMPRINT",EDGE,{"derivedFrom":sQuery(id+"F32.wireOp",EDGE,"E62.bottom")}),-1.0]])]});
            var Q14;
            {var subQ3=sQuery(id+"F32.wireOp",EDGE,"E64.bottom");Q14=makeQuery(id+"F32.imprint","IMPRINT",FACE,{"disambiguationData":[TD([[makeQuery(id+"F32.imprint","IMPRINT",EDGE,{"derivedFrom":subQ3}),-1.0]])]});}
            var Q15;
            Q15=makeQuery(id+"F32.imprint","IMPRINT",FACE,{"disambiguationData":[TD([[makeQuery(id+"F32.imprint","IMPRINT",EDGE,{"derivedFrom":sQuery(id+"F32.wireOp",EDGE,"E66.bottom")}),-1.0]])]});
            extrude(context, id + "F37", {"entities" : qUnion([Q0, Q1, Q2, Q3, Q4, Q5, Q6, Q7, Q8, Q9, Q10, Q11, Q12, Q13, Q14, Q15]), "oppositeDirection" : true, "depth" : 50.8 * mm});
        }
        {
            var Q0;
            Q0=makeQuery(id+"F34.imprint","IMPRINT",FACE,{"disambiguationData":[TD([[makeQuery(id+"F34.imprint","IMPRINT",EDGE,{"derivedFrom":sQuery(id+"F34.wireOp",EDGE,"E81")}),1.0]])]});
            var Q1;
            {var subQ3=sQuery(id+"F36.wireOp",EDGE,"E118.MirrorCS");Q1=makeQuery(id+"F36.imprint","IMPRINT",FACE,{"disambiguationData":[TD([[makeQuery(id+"F36.imprint","IMPRINT",EDGE,{"derivedFrom":subQ3}),-1.0]])]});}
            var Q2;
            {var subQ0=sQuery(id+"F36.wireOp",EDGE,"E106.MirrorCS");Q2=makeQuery(id+"F36.imprint","IMPRINT",FACE,{"disambiguationData":[TD([[makeQuery(id+"F36.imprint","IMPRINT",EDGE,{"derivedFrom":subQ0}),1.0]])]});}
            var Q3;
            Q3=makeQuery(id+"F36.imprint","IMPRINT",FACE,{"disambiguationData":[TD([[makeQuery(id+"F36.imprint","IMPRINT",EDGE,{"derivedFrom":sQuery(id+"F36.wireOp",EDGE,"E103.MirrorCS")}),1.0]])]});
            var Q4;
            Q4=makeQuery(id+"F36.imprint","IMPRINT",FACE,{"disambiguationData":[TD([[makeQuery(id+"F36.imprint","IMPRINT",EDGE,{"derivedFrom":sQuery(id+"F36.wireOp",EDGE,"E101.MirrorCS")}),1.0]])]});
            var Q5;
            {var subQ0=sQuery(id+"F34.wireOp",EDGE,"E88.bottom");Q5=makeQuery(id+"F34.imprint","IMPRINT",FACE,{"disambiguationData":[TD([[makeQuery(id+"F34.imprint","IMPRINT",EDGE,{"derivedFrom":subQ0}),-1.0]])]});}
            var Q6;
            Q6=makeQuery(id+"F34.imprint","IMPRINT",FACE,{"disambiguationData":[TD([[makeQuery(id+"F34.imprint","IMPRINT",EDGE,{"derivedFrom":sQuery(id+"F34.wireOp",EDGE,"E90.bottom")}),-1.0]])]});
            var Q7;
            {var subQ0=sQuery(id+"F34.wireOp",EDGE,"E92.bottom");Q7=makeQuery(id+"F34.imprint","IMPRINT",FACE,{"disambiguationData":[TD([[makeQuery(id+"F34.imprint","IMPRINT",EDGE,{"derivedFrom":subQ0}),-1.0]])]});}
            var Q8;
            {var subQ2=sQuery(id+"F33.wireOp",EDGE,"E72");Q8=makeQuery(id+"F33.imprint","IMPRINT",FACE,{"disambiguationData":[TD([[makeQuery(id+"F33.imprint","IMPRINT",EDGE,{"derivedFrom":subQ2}),1.0]])]});}
            var Q9;
            Q9=makeQuery(id+"F33.imprint","IMPRINT",FACE,{"disambiguationData":[TD([[makeQuery(id+"F33.imprint","IMPRINT",EDGE,{"derivedFrom":sQuery(id+"F33.wireOp",EDGE,"E76.bottom")}),-1.0]])]});
            var Q10;
            {var subQ0=sQuery(id+"F33.wireOp",EDGE,"E78.bottom");Q10=makeQuery(id+"F33.imprint","IMPRINT",FACE,{"disambiguationData":[TD([[makeQuery(id+"F33.imprint","IMPRINT",EDGE,{"derivedFrom":subQ0}),-1.0]])]});}
            var Q11;
            Q11=makeQuery(id+"F33.imprint","IMPRINT",FACE,{"disambiguationData":[TD([[makeQuery(id+"F33.imprint","IMPRINT",EDGE,{"derivedFrom":sQuery(id+"F33.wireOp",EDGE,"E80.bottom")}),-1.0]])]});
            var Q12;
            Q12=makeQuery(id+"F32.imprint","IMPRINT",FACE,{"disambiguationData":[TD([[makeQuery(id+"F32.imprint","IMPRINT",EDGE,{"derivedFrom":sQuery(id+"F32.wireOp",EDGE,"E65.bottom")}),-1.0]])]});
            var Q13;
            {var subQ0=sQuery(id+"F32.wireOp",EDGE,"E63.bottom");Q13=makeQuery(id+"F32.imprint","IMPRINT",FACE,{"disambiguationData":[TD([[makeQuery(id+"F32.imprint","IMPRINT",EDGE,{"derivedFrom":subQ0}),-1.0]])]});}
            var Q14;
            Q14=makeQuery(id+"F32.imprint","IMPRINT",FACE,{"disambiguationData":[TD([[makeQuery(id+"F32.imprint","IMPRINT",EDGE,{"derivedFrom":sQuery(id+"F32.wireOp",EDGE,"E61.bottom")}),-1.0]])]});
            var Q15;
            Q15=makeQuery(id+"F32.imprint","IMPRINT",FACE,{"disambiguationData":[TD([[makeQuery(id+"F32.imprint","IMPRINT",EDGE,{"derivedFrom":sQuery(id+"F32.wireOp",EDGE,"E54")}),1.0]])]});
            extrude(context, id + "F38", {"entities" : qUnion([Q0, Q1, Q2, Q3, Q4, Q5, Q6, Q7, Q8, Q9, Q10, Q11, Q12, Q13, Q14, Q15]), "depth" : 50.8 * mm});
        }
    });
